# Revit family: QF_Kelvinator_738255_KCHST27.8
name_source: partatom
category: Specialty Equipment
units: mm (PartAtom-declared; Revit-internal decimal feet)

## family parameters
Always vertical = Yes
Cut with Voids When Loaded = No
Part Type = Normal
Room Calculation Point = No
Round Connector Dimension = Use Diameter
Shared = No
Work Plane-Based = No

## types (1)
- QF_Kelvinator_738255_KCHST27.8
    Accessory = No
    CO2 Connection Height = 0"
    CO2 Pressure = 0.00 psi
    Chilled Water Return Connection Height = 0"
    Chilled Water Return Size = 0"
    Chilled Water Supply Connection Height = 0"
    Chilled Water Supply Size = 0"
    Cold Water Connection Height = 0"
    Cold Water RI Height = 0"
    Cold Water Size = 0"
    Condensate Return Connection Height = 0"
    Condensate Return Size = 0"
    Cycle = 60 Hz
    Default Elevation = 0"
    Depth = 29 15/16"
    Depth Actual = 760"
    Description = 1-DOOR SANDWICH/SALAD PREP TABLE 29" LONG 6-1/6, 2-1/9 PAN
    Direct Waste Connection Height = 0"
    Direct Waste Size = 0"
    Filtered Water Connection Height = 0"
    Filtered Water Supply Size = 0"
    Foodservice Equipment Identifier = Yes
    Gas Connection Height = 0"
    Gas KW = 0
    Gas Size = 0"
    HP = 0.7 HP
    Height = 43 5/16"
    Height Actual = 1100"
    Hot Water Connection Height = 0"
    Hot Water Flow = 0 GPM
    Hot Water Size = 0"
    Identify Quantity as Lot = Yes
    Indirect Waste Connection Height = 0"
    Indirect Waste Size = 0"
    Item Number = 738255
    Length = 28 15/16"
    Length Actual = 735"
    Manufacturer = Kelvinator
    Model = KCHST27.8
    Phase = 1
    Steam Pounds per Hour = 0
    Steam Supply Connection Height = 0"
    Steam Supply Size = 0"
    Steam Supply Volume = 0 GPM
    URL = KELVINATOR
    URL Cutsheet = www.kelvinatorcommercial.com
    URL Manufacturer = KELVINATOR
    Volts = 115 V
    Watts = 0 W
    Weight = 71.00 lbm
    Weight in Kilograms = 156.528

## geometry (parser evidence)
native form markers: Sweep x8
no freeform markers — native parametric forms only
